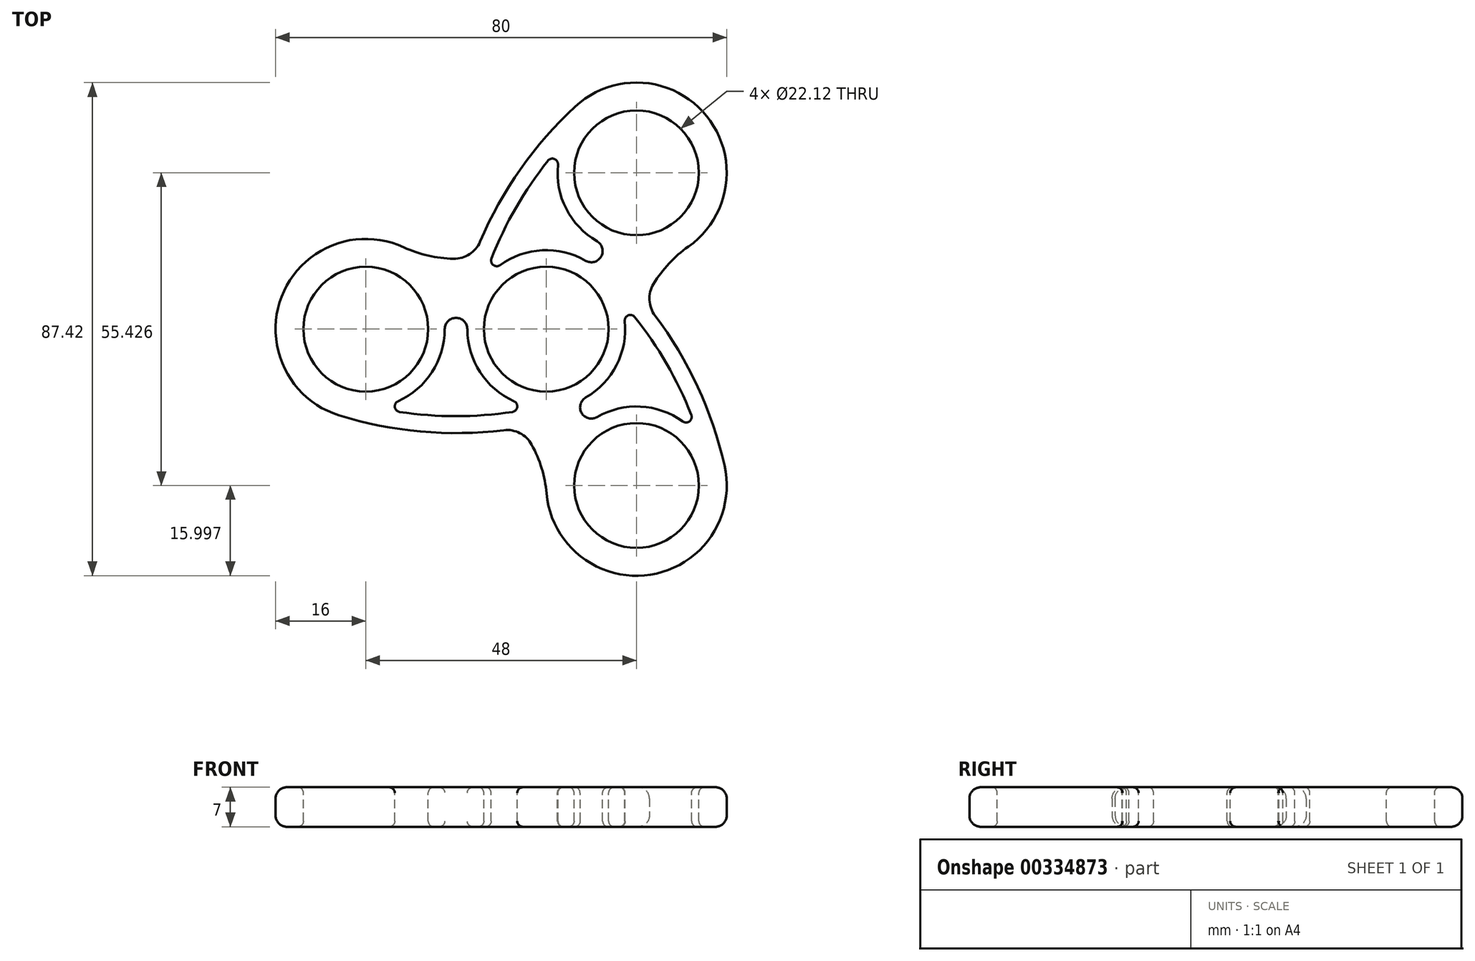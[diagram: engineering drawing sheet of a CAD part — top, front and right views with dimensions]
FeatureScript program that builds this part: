
annotation { "Feature Type Name" : "Feature", "Feature Type Description" : "" }
export const myFeature = defineFeature(function(context is Context, id is Id, definition is map)
    precondition{}
    {
        {
            var Q0;
            Q0=qCreatedBy(makeId("Top.planeOp"),FACE);
            var sketch = newSketch(context, id + "F0", { "sketchPlane" : qUnion([Q0])});
            skArc(sketch, "E0", {"start": v(-25.26, 14.51) * mm, "mid": v(-45.87, 7.97) * mm, "end": v(-41.14, -13.13) * mm});
            skArc(sketch, "E1", {"start": v(-25.26, 14.51) * mm, "mid": v(-20.95, 13.03) * mm, "end": v(-16.43, 12.47) * mm});
            skArc(sketch, "E2.trimOffspring", {"start": v(-41.14, -13.13) * mm, "mid": v(-39.02, -14.38) * mm, "end": v(-36.74, -15.28) * mm});
            skArc(sketch, "E3", {"start": v(-36.74, -15.28) * mm, "mid": v(-22.3, -18.14) * mm, "end": v(-7.57, -17.91) * mm});
            skPoint(sketch, "E4.center.orphan", {"position": v(0, 0) * mm});
            skArc(sketch, "E5.1.0", {"start": v(0.06, -29.13) * mm, "mid": v(16.03, -43.71) * mm, "end": v(31.94, -29.07) * mm});
            skArc(sketch, "E5.1.1", {"start": v(31.6, -24.18) * mm, "mid": v(26.86, -10.24) * mm, "end": v(19.3, 2.4) * mm});
            skArc(sketch, "E5.1.3", {"start": v(0.06, -29.13) * mm, "mid": v(-0.8, -24.66) * mm, "end": v(-2.59, -20.46) * mm});
            skArc(sketch, "E5.1.5", {"start": v(31.94, -29.07) * mm, "mid": v(31.96, -26.6) * mm, "end": v(31.6, -24.18) * mm});
            skArc(sketch, "E5.2.0", {"start": v(25.2, 14.62) * mm, "mid": v(29.84, 35.74) * mm, "end": v(9.2, 42.2) * mm});
            skArc(sketch, "E5.2.1", {"start": v(5.14, 39.46) * mm, "mid": v(-4.56, 28.38) * mm, "end": v(-11.73, 15.51) * mm});
            skArc(sketch, "E5.2.3", {"start": v(25.2, 14.62) * mm, "mid": v(21.76, 11.63) * mm, "end": v(19.01, 8) * mm});
            skArc(sketch, "E5.2.5", {"start": v(9.2, 42.2) * mm, "mid": v(7.06, 40.98) * mm, "end": v(5.14, 39.46) * mm});
            skPoint(sketch, "E6.orphan", {"position": v(-14.35, 8.29) * mm});
            skPoint(sketch, "E7.orphan", {"position": v(14.35, 8.29) * mm});
            skPoint(sketch, "E8.orphan", {"position": v(0, -16.57) * mm});
            skPoint(sketch, "E9.visualSharp", {"position": v(-12.86, 12.7) * mm});
            skArc(sketch, "E9.filletArc", {"start": v(-16.43, 12.47) * mm, "mid": v(-13.62, 13.27) * mm, "end": v(-11.73, 15.51) * mm});
            skPoint(sketch, "E10.visualSharp", {"position": v(17.42, 4.8) * mm});
            skArc(sketch, "E10.filletArc", {"start": v(19.01, 8) * mm, "mid": v(18.3, 5.15) * mm, "end": v(19.3, 2.4) * mm});
            skPoint(sketch, "E11.visualSharp", {"position": v(-4.56, -17.48) * mm});
            skArc(sketch, "E11.filletArc", {"start": v(-2.59, -20.46) * mm, "mid": v(-4.69, -18.43) * mm, "end": v(-7.57, -17.91) * mm});
            skSolve(sketch);
        }
        {
            var Q0;
            Q0=qSketchRegion(id+"F0",true);
            extrude(context, id + "F1", {"entities" : qUnion([Q0]), "depth" : 7 * mm});
        }
        {
            var Q0;
            Q0=makeQuery(id+"F1.opExtrude","CAP_FACE",FACE,{"disambiguationData":[OSD([sQuery(id+"F0.wireOp",EDGE,"E4"),sQuery(id+"F0.wireOp",EDGE,"E0"),sQuery(id+"F0.wireOp",EDGE,"Y62PWa8C-ifkQ-zxFj-Qy6y-K9AmqqDtOzrQ"),sQuery(id+"F0.wireOp",EDGE,"E1"),sQuery(id+"F0.wireOp",EDGE,"U9qsNBJu-XeLE-ORlb-NQLH-GNNNRFqsx3aL"),sQuery(id+"F0.wireOp",EDGE,"KtAAOo4r-4s1N-9Oyr-xdw8-T3c3s2v9GRLw"),sQuery(id+"F0.wireOp",EDGE,"A2y01M4g-3GnU-i1EK-idDg-3enolSD0kJH1"),sQuery(id+"F0.wireOp",EDGE,"06134188-5381-4621-8221-c0cd0b97c355.trimOffspring")])],"isStart":false});
            var sketch = newSketch(context, id + "F2", { "sketchPlane" : qUnion([Q0])});
            skCircle(sketch, "E12", {"center": v(0, 0) * mm, "radius": 11.06 * mm});
            skCircle(sketch, "E13", {"center": v(-32, 0) * mm, "radius": 11.06 * mm});
            skCircle(sketch, "E14.1.0", {"center": v(16, -27.71) * mm, "radius": 11.06 * mm});
            skCircle(sketch, "E14.2.0", {"center": v(16, 27.71) * mm, "radius": 11.06 * mm});
            skSolve(sketch);
        }
        {
            var Q0;
            Q0=qSketchRegion(id+"F2",true);
            extrude(context, id + "F3", {"entities" : qUnion([Q0]), "operationType" : NewBodyOperationType.REMOVE, "endBound" : BoundingType.THROUGH_ALL, "oppositeDirection" : true, "depth" : 25 * mm});
        }
        {
            var Q0;
            Q0=makeQuery(id+"F1.opExtrude","CAP_FACE",FACE,{"disambiguationData":[OSD([sQuery(id+"F0.wireOp",EDGE,"E4"),sQuery(id+"F0.wireOp",EDGE,"E0"),sQuery(id+"F0.wireOp",EDGE,"Y62PWa8C-ifkQ-zxFj-Qy6y-K9AmqqDtOzrQ"),sQuery(id+"F0.wireOp",EDGE,"E1"),sQuery(id+"F0.wireOp",EDGE,"A2y01M4g-3GnU-i1EK-idDg-3enolSD0kJH1"),sQuery(id+"F0.wireOp",EDGE,"06134188-5381-4621-8221-c0cd0b97c355.trimOffspring"),sQuery(id+"F0.wireOp",EDGE,"hpOvTq7A-kyfb-DXtC-TEhA-or5gheuMUULX"),sQuery(id+"F0.wireOp",EDGE,"wBePiWC6-iGpO-Zq4v-ABb4-8q9CdOJLcKBH"),sQuery(id+"F0.wireOp",EDGE,"ZJYLghvL-pm70-bnTZ-rQ5k-KHeNHSjt74Mt"),sQuery(id+"F0.wireOp",EDGE,"E2.trimOffspring"),sQuery(id+"F0.wireOp",EDGE,"bhJmbQDj-123R-5zu5-01mg-wOOI3Yt0Lu7z"),sQuery(id+"F0.wireOp",EDGE,"YeVEtyaY-yGgt-7S4g-LW9z-fGMiD1Vh3O3b"),sQuery(id+"F0.wireOp",EDGE,"oH4s39by-uDe5-ougK-N1i2-lCchJTmDNlGg"),sQuery(id+"F0.wireOp",EDGE,"a8a12002-a156-4083-88be-4161392d71c2.trimOffspring"),sQuery(id+"F0.wireOp",EDGE,"ue8C1jBA-TXoT-IyUg-P85N-IvGPrk7CsN6a"),sQuery(id+"F0.wireOp",EDGE,"E3")])],"isStart":false});
            var sketch = newSketch(context, id + "F4", { "sketchPlane" : qUnion([Q0])});
            skArc(sketch, "E15", {"start": v(-26, -14.67) * mm, "mid": v(-16, -15.42) * mm, "end": v(-6, -14.67) * mm});
            skArc(sketch, "E16", {"start": v(-14, 0) * mm, "mid": v(-11.75, -7.6) * mm, "end": v(-5.73, -12.77) * mm});
            skArc(sketch, "E17", {"start": v(-14, 0) * mm, "mid": v(-16, 2) * mm, "end": v(-18, 0) * mm});
            skArc(sketch, "E18.trimOffspring", {"start": v(-26.27, -12.77) * mm, "mid": v(-20.25, -7.6) * mm, "end": v(-18, 0) * mm});
            skPoint(sketch, "E19.visualSharp", {"position": v(-30.25, -13.9) * mm});
            skArc(sketch, "E19.filletArc", {"start": v(-26.27, -12.77) * mm, "mid": v(-26.85, -13.82) * mm, "end": v(-26, -14.67) * mm});
            skPoint(sketch, "E20.visualSharp", {"position": v(-1.75, -13.9) * mm});
            skArc(sketch, "E20.filletArc", {"start": v(-6, -14.67) * mm, "mid": v(-5.15, -13.82) * mm, "end": v(-5.73, -12.77) * mm});
            skArc(sketch, "E21.1.0", {"start": v(24.2, -16.36) * mm, "mid": v(16.71, -13.73) * mm, "end": v(9, -15.59) * mm});
            skPoint(sketch, "E21.1.1", {"position": v(27.16, -19.26) * mm});
            skArc(sketch, "E21.1.2", {"start": v(7, -12.12) * mm, "mid": v(12.47, -6.37) * mm, "end": v(13.93, 1.42) * mm});
            skArc(sketch, "E21.1.3", {"start": v(25.71, -15.19) * mm, "mid": v(21.36, -6.14) * mm, "end": v(15.7, 2.15) * mm});
            skPoint(sketch, "E21.1.4", {"position": v(12.9, 5.43) * mm});
            skArc(sketch, "E21.1.5", {"start": v(7, -12.12) * mm, "mid": v(6.27, -14.85) * mm, "end": v(9, -15.59) * mm});
            skArc(sketch, "E21.1.6", {"start": v(24.2, -16.36) * mm, "mid": v(25.4, -16.34) * mm, "end": v(25.71, -15.19) * mm});
            skArc(sketch, "E21.1.7", {"start": v(15.7, 2.15) * mm, "mid": v(14.54, 2.45) * mm, "end": v(13.93, 1.42) * mm});
            skPoint(sketch, "E21.1.8", {"position": v(16, -27.71) * mm});
            skArc(sketch, "E21.2.0", {"start": v(2.07, 29.13) * mm, "mid": v(3.53, 21.34) * mm, "end": v(9, 15.59) * mm});
            skPoint(sketch, "E21.2.1", {"position": v(3.1, 33.15) * mm});
            skArc(sketch, "E21.2.2", {"start": v(7, 12.13) * mm, "mid": v(-0.71, 13.98) * mm, "end": v(-8.2, 11.35) * mm});
            skArc(sketch, "E21.2.3", {"start": v(0.3, 29.86) * mm, "mid": v(-5.36, 21.57) * mm, "end": v(-9.71, 12.53) * mm});
            skPoint(sketch, "E21.2.4", {"position": v(-11.16, 8.46) * mm});
            skArc(sketch, "E21.2.5", {"start": v(7, 12.13) * mm, "mid": v(9.73, 12.86) * mm, "end": v(9, 15.59) * mm});
            skArc(sketch, "E21.2.6", {"start": v(2.07, 29.13) * mm, "mid": v(1.46, 30.16) * mm, "end": v(0.3, 29.86) * mm});
            skArc(sketch, "E21.2.7", {"start": v(-9.71, 12.53) * mm, "mid": v(-9.4, 11.37) * mm, "end": v(-8.2, 11.35) * mm});
            skPoint(sketch, "E21.2.8", {"position": v(16, 27.71) * mm});
            skSolve(sketch);
        }
        {
            var Q0;
            Q0=qSketchRegion(id+"F4",true);
            extrude(context, id + "F5", {"entities" : qUnion([Q0]), "operationType" : NewBodyOperationType.REMOVE, "endBound" : BoundingType.THROUGH_ALL, "oppositeDirection" : true, "depth" : 25 * mm});
        }
        {
            var Q0;
            Q0=makeQuery(id+"F1.opExtrude","SWEPT_FACE",FACE,{"disambiguationData":[OSD([sQuery(id+"F0.wireOp",EDGE,"E5.1.1")])]});
            var Q1;
            Q1=makeQuery(id+"F1.opExtrude","SWEPT_FACE",FACE,{"disambiguationData":[OSD([sQuery(id+"F0.wireOp",EDGE,"E10.filletArc")])]});
            var Q2;
            Q2=makeQuery(id+"F1.opExtrude","SWEPT_FACE",FACE,{"disambiguationData":[OSD([sQuery(id+"F0.wireOp",EDGE,"E5.2.3")])]});
            var Q3;
            Q3=makeQuery(id+"F1.opExtrude","SWEPT_FACE",FACE,{"disambiguationData":[OSD([sQuery(id+"F0.wireOp",EDGE,"E5.2.0"),sQuery(id+"F0.wireOp",EDGE,"E5.2.5")])]});
            var Q4;
            Q4=makeQuery(id+"F1.opExtrude","SWEPT_FACE",FACE,{"disambiguationData":[OSD([sQuery(id+"F0.wireOp",EDGE,"E5.1.0"),sQuery(id+"F0.wireOp",EDGE,"E5.1.5")])]});
            var Q5;
            Q5=makeQuery(id+"F1.opExtrude","SWEPT_FACE",FACE,{"disambiguationData":[OSD([sQuery(id+"F0.wireOp",EDGE,"E5.1.3")])]});
            var Q6;
            Q6=makeQuery(id+"F1.opExtrude","SWEPT_FACE",FACE,{"disambiguationData":[OSD([sQuery(id+"F0.wireOp",EDGE,"E11.filletArc")])]});
            var Q7;
            Q7=makeQuery(id+"F1.opExtrude","SWEPT_FACE",FACE,{"disambiguationData":[OSD([sQuery(id+"F0.wireOp",EDGE,"E3")])]});
            var Q8;
            Q8=makeQuery(id+"F1.opExtrude","SWEPT_FACE",FACE,{"disambiguationData":[OSD([sQuery(id+"F0.wireOp",EDGE,"E0"),sQuery(id+"F0.wireOp",EDGE,"E2.trimOffspring")])]});
            var Q9;
            Q9=makeQuery(id+"F1.opExtrude","SWEPT_FACE",FACE,{"disambiguationData":[OSD([sQuery(id+"F0.wireOp",EDGE,"E5.2.1")])]});
            var Q10;
            Q10=makeQuery(id+"F1.opExtrude","SWEPT_FACE",FACE,{"disambiguationData":[OSD([sQuery(id+"F0.wireOp",EDGE,"E9.filletArc")])]});
            var Q11;
            Q11=makeQuery(id+"F1.opExtrude","SWEPT_FACE",FACE,{"disambiguationData":[OSD([sQuery(id+"F0.wireOp",EDGE,"E1")])]});
            fillet(context, id + "F6", {"entities" : qUnion([Q0, Q1, Q2, Q3, Q4, Q5, Q6, Q7, Q8, Q9, Q10, Q11]), "radius" : 2 * mm, "tangentPropagation" : true, "allowEdgeOverflow" : false});
        }
        {
            var Q0;
            Q0=makeQuery(id+"F3.boolean.opBoolean","COPY",FACE,{"derivedFrom":makeQuery(id+"F3.opExtrude","SWEPT_FACE",FACE,{"disambiguationData":[OSD([sQuery(id+"F2.wireOp",EDGE,"E14.2.0")])]})});
            var Q1;
            Q1=makeQuery(id+"F3.boolean.opBoolean","COPY",FACE,{"derivedFrom":makeQuery(id+"F3.opExtrude","SWEPT_FACE",FACE,{"disambiguationData":[OSD([sQuery(id+"F2.wireOp",EDGE,"E12")])]})});
            var Q2;
            Q2=makeQuery(id+"F3.boolean.opBoolean","COPY",FACE,{"derivedFrom":makeQuery(id+"F3.opExtrude","SWEPT_FACE",FACE,{"disambiguationData":[OSD([sQuery(id+"F2.wireOp",EDGE,"E14.1.0")])]})});
            var Q3;
            Q3=makeQuery(id+"F3.boolean.opBoolean","COPY",FACE,{"derivedFrom":makeQuery(id+"F3.opExtrude","SWEPT_FACE",FACE,{"disambiguationData":[OSD([sQuery(id+"F2.wireOp",EDGE,"E13")])]})});
            fillet(context, id + "F7", {"entities" : qUnion([Q0, Q1, Q2, Q3]), "radius" : 1 * mm, "tangentPropagation" : true, "allowEdgeOverflow" : false});
        }
        {
            var Q0;
            Q0=makeQuery(id+"F5.boolean.opBoolean","COPY",FACE,{"derivedFrom":makeQuery(id+"F5.opExtrude","SWEPT_FACE",FACE,{"disambiguationData":[OSD([sQuery(id+"F4.wireOp",EDGE,"E21.2.0")])]})});
            var Q1;
            Q1=makeQuery(id+"F5.boolean.opBoolean","COPY",FACE,{"derivedFrom":makeQuery(id+"F5.opExtrude","SWEPT_FACE",FACE,{"disambiguationData":[OSD([sQuery(id+"F4.wireOp",EDGE,"E21.1.3")])]})});
            var Q2;
            Q2=makeQuery(id+"F5.boolean.opBoolean","COPY",FACE,{"derivedFrom":makeQuery(id+"F5.opExtrude","SWEPT_FACE",FACE,{"disambiguationData":[OSD([sQuery(id+"F4.wireOp",EDGE,"E16")])]})});
            var Q3;
            Q3=makeQuery(id+"F5.boolean.opBoolean","COPY",FACE,{"derivedFrom":makeQuery(id+"F5.opExtrude","SWEPT_FACE",FACE,{"disambiguationData":[OSD([sQuery(id+"F4.wireOp",EDGE,"E21.2.5")])]})});
            var Q4;
            Q4=makeQuery(id+"F5.boolean.opBoolean","COPY",FACE,{"derivedFrom":makeQuery(id+"F5.opExtrude","SWEPT_FACE",FACE,{"disambiguationData":[OSD([sQuery(id+"F4.wireOp",EDGE,"E17")])]})});
            var Q5;
            Q5=makeQuery(id+"F5.boolean.opBoolean","COPY",FACE,{"derivedFrom":makeQuery(id+"F5.opExtrude","SWEPT_FACE",FACE,{"disambiguationData":[OSD([sQuery(id+"F4.wireOp",EDGE,"E21.2.3")])]})});
            var Q6;
            Q6=makeQuery(id+"F5.boolean.opBoolean","COPY",FACE,{"derivedFrom":makeQuery(id+"F5.opExtrude","SWEPT_FACE",FACE,{"disambiguationData":[OSD([sQuery(id+"F4.wireOp",EDGE,"E21.1.2")])]})});
            var Q7;
            Q7=makeQuery(id+"F5.boolean.opBoolean","COPY",FACE,{"derivedFrom":makeQuery(id+"F5.opExtrude","SWEPT_FACE",FACE,{"disambiguationData":[OSD([sQuery(id+"F4.wireOp",EDGE,"E21.1.7")])]})});
            var Q8;
            Q8=makeQuery(id+"F5.boolean.opBoolean","COPY",FACE,{"derivedFrom":makeQuery(id+"F5.opExtrude","SWEPT_FACE",FACE,{"disambiguationData":[OSD([sQuery(id+"F4.wireOp",EDGE,"E21.2.6")])]})});
            var Q9;
            Q9=makeQuery(id+"F5.boolean.opBoolean","COPY",FACE,{"derivedFrom":makeQuery(id+"F5.opExtrude","SWEPT_FACE",FACE,{"disambiguationData":[OSD([sQuery(id+"F4.wireOp",EDGE,"E18.trimOffspring")])]})});
            var Q10;
            Q10=makeQuery(id+"F5.boolean.opBoolean","COPY",FACE,{"derivedFrom":makeQuery(id+"F5.opExtrude","SWEPT_FACE",FACE,{"disambiguationData":[OSD([sQuery(id+"F4.wireOp",EDGE,"E21.1.5")])]})});
            var Q11;
            Q11=makeQuery(id+"F5.boolean.opBoolean","COPY",FACE,{"derivedFrom":makeQuery(id+"F5.opExtrude","SWEPT_FACE",FACE,{"disambiguationData":[OSD([sQuery(id+"F4.wireOp",EDGE,"E21.2.2")])]})});
            var Q12;
            Q12=makeQuery(id+"F5.boolean.opBoolean","COPY",FACE,{"derivedFrom":makeQuery(id+"F5.opExtrude","SWEPT_FACE",FACE,{"disambiguationData":[OSD([sQuery(id+"F4.wireOp",EDGE,"E21.1.0")])]})});
            var Q13;
            Q13=makeQuery(id+"F5.boolean.opBoolean","COPY",FACE,{"derivedFrom":makeQuery(id+"F5.opExtrude","SWEPT_FACE",FACE,{"disambiguationData":[OSD([sQuery(id+"F4.wireOp",EDGE,"E21.1.6")])]})});
            var Q14;
            Q14=makeQuery(id+"F5.boolean.opBoolean","COPY",FACE,{"derivedFrom":makeQuery(id+"F5.opExtrude","SWEPT_FACE",FACE,{"disambiguationData":[OSD([sQuery(id+"F4.wireOp",EDGE,"E21.2.7")])]})});
            var Q15;
            Q15=makeQuery(id+"F5.boolean.opBoolean","COPY",FACE,{"derivedFrom":makeQuery(id+"F5.opExtrude","SWEPT_FACE",FACE,{"disambiguationData":[OSD([sQuery(id+"F4.wireOp",EDGE,"E15")])]})});
            var Q16;
            Q16=makeQuery(id+"F5.boolean.opBoolean","COPY",FACE,{"derivedFrom":makeQuery(id+"F5.opExtrude","SWEPT_FACE",FACE,{"disambiguationData":[OSD([sQuery(id+"F4.wireOp",EDGE,"E20.filletArc")])]})});
            var Q17;
            Q17=makeQuery(id+"F5.boolean.opBoolean","COPY",FACE,{"derivedFrom":makeQuery(id+"F5.opExtrude","SWEPT_FACE",FACE,{"disambiguationData":[OSD([sQuery(id+"F4.wireOp",EDGE,"E19.filletArc")])]})});
            fillet(context, id + "F8", {"entities" : qUnion([Q0, Q1, Q2, Q3, Q4, Q5, Q6, Q7, Q8, Q9, Q10, Q11, Q12, Q13, Q14, Q15, Q16, Q17]), "radius" : 1 * mm, "tangentPropagation" : true, "allowEdgeOverflow" : false});
        }
    });
